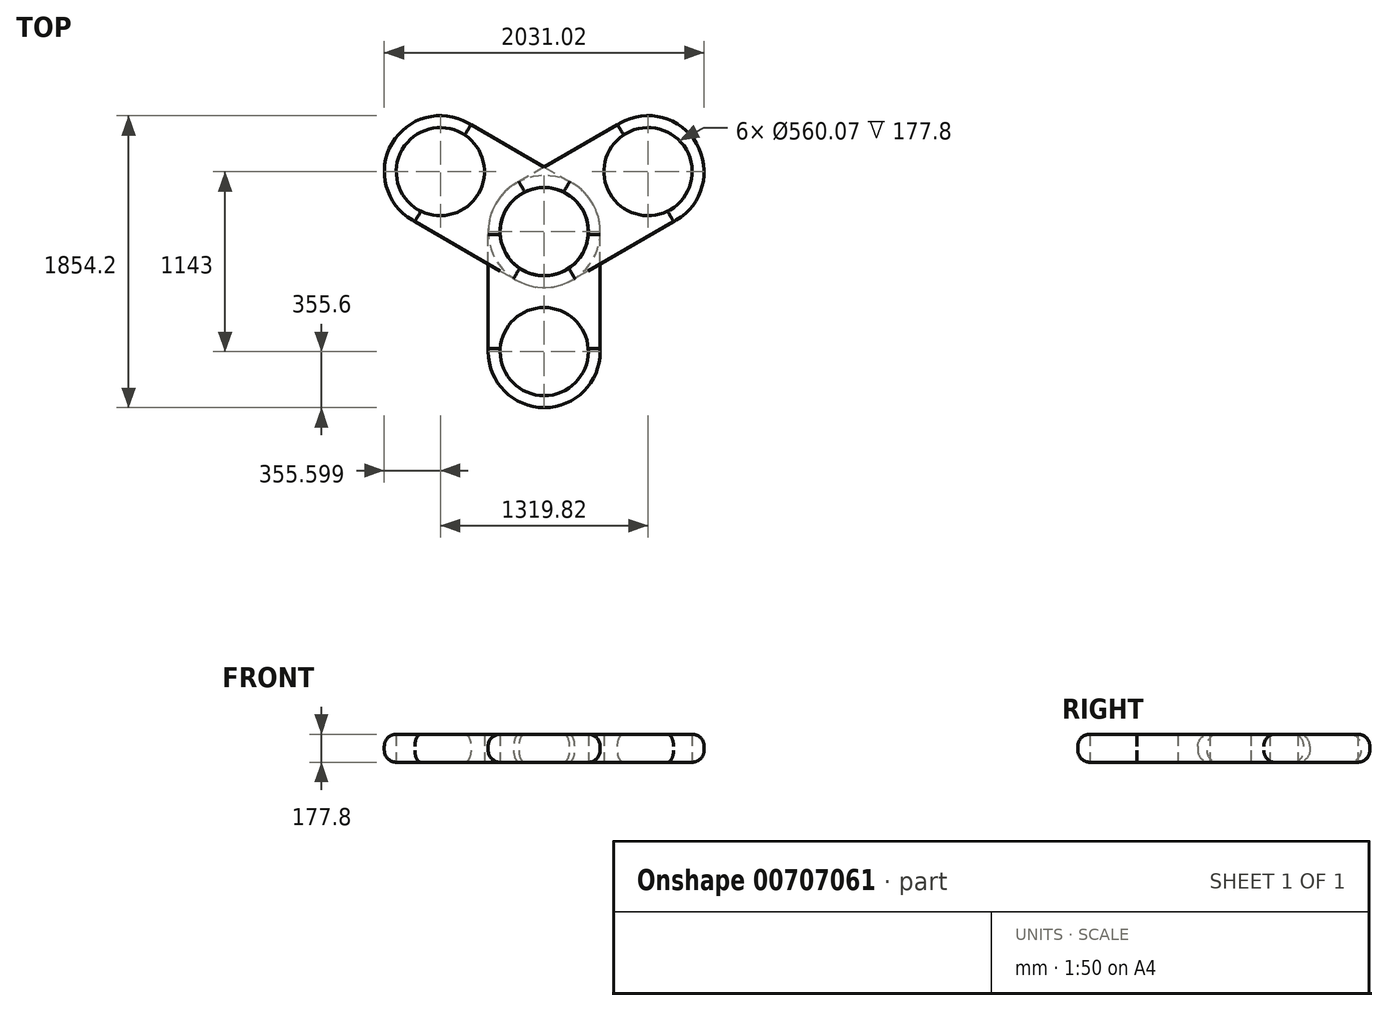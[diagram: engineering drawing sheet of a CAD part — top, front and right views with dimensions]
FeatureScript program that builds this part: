
annotation { "Feature Type Name" : "Feature", "Feature Type Description" : "" }
export const myFeature = defineFeature(function(context is Context, id is Id, definition is map)
    precondition{}
    {
        {
            var Q0;
            Q0=qCreatedBy(makeId("Top.planeOp"),FACE);
            var sketch = newSketch(context, id + "F0", { "sketchPlane" : qUnion([Q0])});
            skLineSegment(sketch, "E0.bottom", {"start": v(0, 0) * mm, "end": v(711.2, 0) * mm});
            skLineSegment(sketch, "E0.top", {"start": v(0, 762) * mm, "end": v(711.2, 762) * mm});
            skLineSegment(sketch, "E0.left", {"start": v(0, 0) * mm, "end": v(0, 762) * mm});
            skLineSegment(sketch, "E0.right", {"start": v(711.2, 0) * mm, "end": v(711.2, 762) * mm});
            skCircle(sketch, "E1", {"center": v(355.6, 762) * mm, "radius": 355.6 * mm});
            skCircle(sketch, "E2", {"center": v(355.6, 762) * mm, "radius": 280.04 * mm});
            skCircle(sketch, "E3", {"center": v(355.6, 0) * mm, "radius": 355.6 * mm});
            skCircle(sketch, "E4", {"center": v(355.6, 0) * mm, "radius": 280.04 * mm});
            skSolve(sketch);
        }
        {
            var Q0;
            {var subQ1=sQuery(id+"F0.wireOp",EDGE,"E0.bottom");var subQ3=sQuery(id+"F0.wireOp",EDGE,"E4");var subQ4=makeQuery(id+"F0.imprint","INTERSECT",VERTEX,{"disambiguationData":[OD(0.0)],"derivedFrom":[subQ1,subQ3]});Q0=makeQuery(id+"F0.imprint","IMPRINT",FACE,{"disambiguationData":[TD([[makeQuery(id+"F0.imprint","IMPRINT",EDGE,{"disambiguationData":[TD([[subQ4,-1.0]])],"derivedFrom":subQ3}),-1.0]])]});}
            var Q1;
            {var subQ1=sQuery(id+"F0.wireOp",EDGE,"E0.bottom");var subQ3=sQuery(id+"F0.wireOp",EDGE,"E4");var subQ4=makeQuery(id+"F0.imprint","INTERSECT",VERTEX,{"disambiguationData":[OD(0.0)],"derivedFrom":[subQ1,subQ3]});Q1=makeQuery(id+"F0.imprint","IMPRINT",FACE,{"disambiguationData":[TD([[makeQuery(id+"F0.imprint","IMPRINT",EDGE,{"disambiguationData":[TD([[subQ4,1.0]])],"derivedFrom":subQ3}),-1.0]])]});}
            var Q2;
            {var subQ0=sQuery(id+"F0.wireOp",EDGE,"E0.left");Q2=makeQuery(id+"F0.imprint","IMPRINT",FACE,{"disambiguationData":[TD([[makeQuery(id+"F0.imprint","IMPRINT",EDGE,{"derivedFrom":subQ0}),-1.0]])]});}
            var Q3;
            {var subQ1=sQuery(id+"F0.wireOp",EDGE,"E0.top");var subQ3=sQuery(id+"F0.wireOp",EDGE,"E2");var subQ4=makeQuery(id+"F0.imprint","INTERSECT",VERTEX,{"disambiguationData":[OD(0.0)],"derivedFrom":[subQ1,subQ3]});Q3=makeQuery(id+"F0.imprint","IMPRINT",FACE,{"disambiguationData":[TD([[makeQuery(id+"F0.imprint","IMPRINT",EDGE,{"disambiguationData":[TD([[subQ4,1.0]])],"derivedFrom":subQ3}),-1.0]])]});}
            var Q4;
            {var subQ1=sQuery(id+"F0.wireOp",EDGE,"E0.top");var subQ3=sQuery(id+"F0.wireOp",EDGE,"E2");var subQ4=makeQuery(id+"F0.imprint","INTERSECT",VERTEX,{"disambiguationData":[OD(0.0)],"derivedFrom":[subQ1,subQ3]});Q4=makeQuery(id+"F0.imprint","IMPRINT",FACE,{"disambiguationData":[TD([[makeQuery(id+"F0.imprint","IMPRINT",EDGE,{"disambiguationData":[TD([[subQ4,-1.0]])],"derivedFrom":subQ3}),-1.0]])]});}
            extrude(context, id + "F1", {"entities" : qUnion([Q0, Q1, Q2, Q3, Q4]), "depth" : 177.8 * mm, "offsetDistance" : 25.4 * mm});
        }
        {
            var Q0;
            Q0=makeQuery(id+"F1.opExtrude","SWEPT_BODY",BODY,{"disambiguationData":[OSD([sQuery(id+"F0.wireOp",EDGE,"E0.left"),sQuery(id+"F0.wireOp",EDGE,"E0.right"),sQuery(id+"F0.wireOp",EDGE,"E1"),sQuery(id+"F0.wireOp",EDGE,"E2"),sQuery(id+"F0.wireOp",EDGE,"E3"),sQuery(id+"F0.wireOp",EDGE,"E4")])]});
            var Q1;
            Q1=makeQuery(id+"F1.opExtrude","SWEPT_FACE",FACE,{"disambiguationData":[OSD([sQuery(id+"F0.wireOp",EDGE,"E1")])]});
            circularPattern(context, id + "F2", {"entities" : qUnion([Q0]), "axis" : qUnion([Q1]), "angle" : 360 * degree, "instanceCount" : 3, "equalSpace" : true});
        }
        {
            var Q0;
            Q0=makeQuery(id+"F2.opPattern","COPY",EDGE,{"derivedFrom":makeQuery(id+"F1.opExtrude","CAP_EDGE",EDGE,{"disambiguationData":[OSD([sQuery(id+"F0.wireOp",EDGE,"E0.left")])],"isStart":false}),"instanceName":"2"});
            var Q1;
            Q1=makeQuery(id+"F2.opPattern","COPY",EDGE,{"derivedFrom":makeQuery(id+"F1.opExtrude","CAP_EDGE",EDGE,{"disambiguationData":[OSD([sQuery(id+"F0.wireOp",EDGE,"E0.left")])],"isStart":true}),"instanceName":"2"});
            var Q2;
            Q2=makeQuery(id+"F1.opExtrude","CAP_EDGE",EDGE,{"disambiguationData":[OSD([sQuery(id+"F0.wireOp",EDGE,"E0.right")])],"isStart":false});
            var Q3;
            Q3=makeQuery(id+"F1.opExtrude","CAP_EDGE",EDGE,{"disambiguationData":[OSD([sQuery(id+"F0.wireOp",EDGE,"E0.right")])],"isStart":true});
            var Q4;
            Q4=makeQuery(id+"F1.opExtrude","CAP_EDGE",EDGE,{"disambiguationData":[OSD([sQuery(id+"F0.wireOp",EDGE,"E3")])],"isStart":false});
            var Q5;
            Q5=makeQuery(id+"F1.opExtrude","CAP_EDGE",EDGE,{"disambiguationData":[OSD([sQuery(id+"F0.wireOp",EDGE,"E3")])],"isStart":true});
            var Q6;
            Q6=makeQuery(id+"F1.opExtrude","CAP_EDGE",EDGE,{"disambiguationData":[OSD([sQuery(id+"F0.wireOp",EDGE,"E0.left")])],"isStart":false});
            var Q7;
            Q7=makeQuery(id+"F1.opExtrude","CAP_EDGE",EDGE,{"disambiguationData":[OSD([sQuery(id+"F0.wireOp",EDGE,"E0.left")])],"isStart":true});
            var Q8;
            Q8=makeQuery(id+"F2.opPattern","COPY",EDGE,{"derivedFrom":makeQuery(id+"F1.opExtrude","CAP_EDGE",EDGE,{"disambiguationData":[OSD([sQuery(id+"F0.wireOp",EDGE,"E0.right")])],"isStart":false}),"instanceName":"1"});
            var Q9;
            Q9=makeQuery(id+"F2.opPattern","COPY",EDGE,{"derivedFrom":makeQuery(id+"F1.opExtrude","CAP_EDGE",EDGE,{"disambiguationData":[OSD([sQuery(id+"F0.wireOp",EDGE,"E0.right")])],"isStart":true}),"instanceName":"1"});
            var Q10;
            Q10=makeQuery(id+"F2.opPattern","COPY",EDGE,{"derivedFrom":makeQuery(id+"F1.opExtrude","CAP_EDGE",EDGE,{"disambiguationData":[OSD([sQuery(id+"F0.wireOp",EDGE,"E3")])],"isStart":true}),"instanceName":"1"});
            var Q11;
            Q11=makeQuery(id+"F2.opPattern","COPY",EDGE,{"derivedFrom":makeQuery(id+"F1.opExtrude","CAP_EDGE",EDGE,{"disambiguationData":[OSD([sQuery(id+"F0.wireOp",EDGE,"E3")])],"isStart":false}),"instanceName":"1"});
            var Q12;
            Q12=makeQuery(id+"F2.opPattern","COPY",EDGE,{"derivedFrom":makeQuery(id+"F1.opExtrude","CAP_EDGE",EDGE,{"disambiguationData":[OSD([sQuery(id+"F0.wireOp",EDGE,"E0.left")])],"isStart":false}),"instanceName":"1"});
            var Q13;
            Q13=makeQuery(id+"F2.opPattern","COPY",EDGE,{"derivedFrom":makeQuery(id+"F1.opExtrude","CAP_EDGE",EDGE,{"disambiguationData":[OSD([sQuery(id+"F0.wireOp",EDGE,"E0.left")])],"isStart":true}),"instanceName":"1"});
            var Q14;
            Q14=makeQuery(id+"F2.opPattern","COPY",EDGE,{"derivedFrom":makeQuery(id+"F1.opExtrude","CAP_EDGE",EDGE,{"disambiguationData":[OSD([sQuery(id+"F0.wireOp",EDGE,"E0.right")])],"isStart":false}),"instanceName":"2"});
            var Q15;
            Q15=makeQuery(id+"F2.opPattern","COPY",EDGE,{"derivedFrom":makeQuery(id+"F1.opExtrude","CAP_EDGE",EDGE,{"disambiguationData":[OSD([sQuery(id+"F0.wireOp",EDGE,"E0.right")])],"isStart":true}),"instanceName":"2"});
            var Q16;
            Q16=makeQuery(id+"F2.opPattern","COPY",EDGE,{"derivedFrom":makeQuery(id+"F1.opExtrude","CAP_EDGE",EDGE,{"disambiguationData":[OSD([sQuery(id+"F0.wireOp",EDGE,"E3")])],"isStart":false}),"instanceName":"2"});
            var Q17;
            Q17=makeQuery(id+"F2.opPattern","COPY",EDGE,{"derivedFrom":makeQuery(id+"F1.opExtrude","CAP_EDGE",EDGE,{"disambiguationData":[OSD([sQuery(id+"F0.wireOp",EDGE,"E3")])],"isStart":true}),"instanceName":"2"});
            fillet(context, id + "F3", {"entities" : qUnion([Q0, Q1, Q2, Q3, Q4, Q5, Q6, Q7, Q8, Q9, Q10, Q11, Q12, Q13, Q14, Q15, Q16, Q17]), "radius" : 76.2 * mm, "tangentPropagation" : true, "allowEdgeOverflow" : false});
        }
    });
